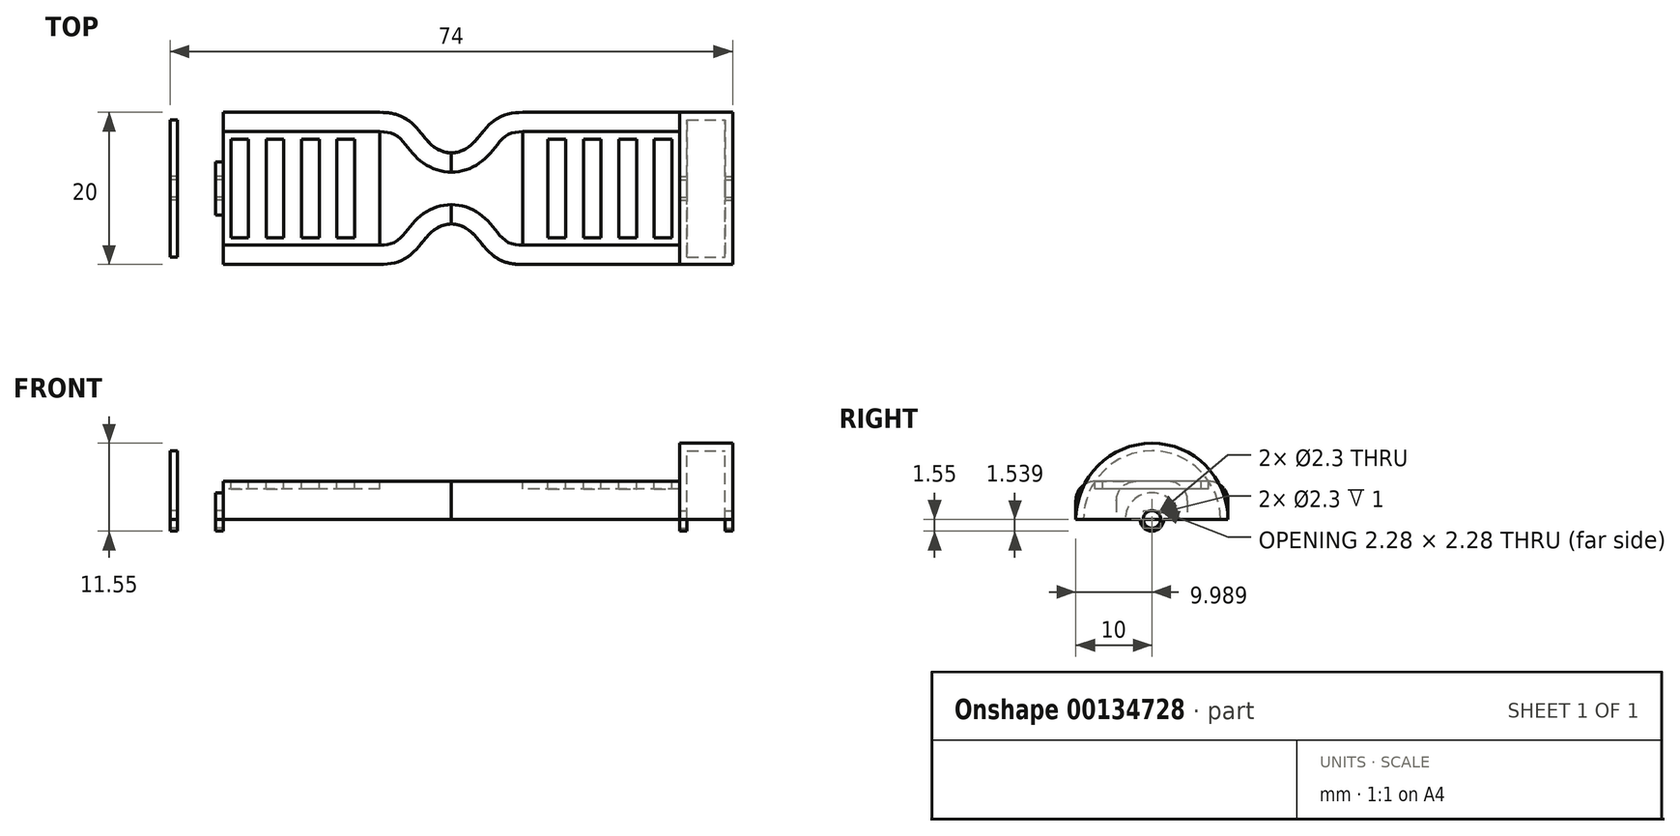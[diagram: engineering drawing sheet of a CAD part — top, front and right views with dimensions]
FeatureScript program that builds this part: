
annotation { "Feature Type Name" : "Feature", "Feature Type Description" : "" }
export const myFeature = defineFeature(function(context is Context, id is Id, definition is map)
    precondition{}
    {
        {
            var Q0;
            Q0=qCreatedBy(makeId("Top.planeOp"),FACE);
            var sketch = newSketch(context, id + "F0", { "sketchPlane" : qUnion([Q0])});
            skLineSegment(sketch, "E0.bottom", {"start": v(37, 10) * mm, "end": v(-37, 10) * mm});
            skLineSegment(sketch, "E0.top", {"start": v(37, -10) * mm, "end": v(-37, -10) * mm});
            skLineSegment(sketch, "E0.left", {"start": v(37, 10) * mm, "end": v(37, -10) * mm});
            skLineSegment(sketch, "E0.right", {"start": v(-37, 10) * mm, "end": v(-37, -10) * mm});
            skPoint(sketch, "E0.middle", {"position": v(0, 0) * mm});
            skLineSegment(sketch, "E1", {"start": v(30, 10) * mm, "end": v(30, -10) * mm});
            skLineSegment(sketch, "E2.MirrorCS", {"start": v(-30, 10) * mm, "end": v(-30, -10) * mm});
            skLineSegment(sketch, "E3", {"start": v(-9.38, 10) * mm, "end": v(-9.38, -10) * mm});
            skLineSegment(sketch, "E4.MirrorCS", {"start": v(9.38, 10) * mm, "end": v(9.38, -10) * mm});
            skFitSpline(sketch, "E5", {"points": [v(-9.38, 10) * mm, v(0, 4.67) * mm], "startDerivative": vector(17.64, 0) * mm, "endDerivative": vector(12.98, -0.7) * mm});
            skFitSpline(sketch, "E6.MirrorCS", {"points": [v(-9.38, -10) * mm, v(0, -4.67) * mm], "startDerivative": vector(17.64, 0) * mm, "endDerivative": vector(12.98, 0.7) * mm});
            skFitSpline(sketch, "E7.MirrorCS", {"points": [v(9.38, 10) * mm, v(0, 4.67) * mm], "startDerivative": vector(-17.64, 0) * mm, "endDerivative": vector(-12.98, -0.7) * mm});
            skFitSpline(sketch, "E8.MirrorCS", {"points": [v(9.38, -10) * mm, v(0, -4.67) * mm], "startDerivative": vector(-17.64, 0) * mm, "endDerivative": vector(-12.98, 0.7) * mm});
            skLineSegment(sketch, "E9", {"start": v(-37, 10) * mm, "end": v(-30, 10) * mm});
            skLineSegment(sketch, "E10", {"start": v(-30, -10) * mm, "end": v(-37, -10) * mm});
            skLineSegment(sketch, "E11.0", {"start": v(-31, -9) * mm, "end": v(-37, -9) * mm});
            skLineSegment(sketch, "E11.1", {"start": v(-31, 9) * mm, "end": v(-31, -9) * mm});
            skLineSegment(sketch, "E11.2", {"start": v(-37, 9) * mm, "end": v(-31, 9) * mm});
            skLineSegment(sketch, "E12", {"start": v(-36, 9) * mm, "end": v(-36, -9) * mm});
            skLineSegment(sketch, "E13.MirrorCS", {"start": v(36, 9) * mm, "end": v(36, -9) * mm});
            skLineSegment(sketch, "E14.MirrorCS", {"start": v(37, 9) * mm, "end": v(31, 9) * mm});
            skLineSegment(sketch, "E15.MirrorCS", {"start": v(31, 9) * mm, "end": v(31, -9) * mm});
            skLineSegment(sketch, "E16.MirrorCS", {"start": v(31, -9) * mm, "end": v(37, -9) * mm});
            skLineSegment(sketch, "E17", {"start": v(-37, 0) * mm, "end": v(37, 0) * mm});
            skLineSegment(sketch, "E18", {"start": v(-31, -3.5) * mm, "end": v(-16, -3.5) * mm});
            skLineSegment(sketch, "E19", {"start": v(-16, -3.5) * mm, "end": v(-16, 0) * mm});
            skLineSegment(sketch, "E20", {"start": v(-31, 0) * mm, "end": v(-31, -3.5) * mm});
            skLineSegment(sketch, "E21.MirrorCS", {"start": v(-31, 3.5) * mm, "end": v(-16, 3.5) * mm});
            skLineSegment(sketch, "E22.MirrorCS", {"start": v(-16, 3.5) * mm, "end": v(-16, 0) * mm});
            skLineSegment(sketch, "E23.MirrorCS", {"start": v(31, -3.5) * mm, "end": v(16, -3.5) * mm});
            skLineSegment(sketch, "E24.MirrorCS", {"start": v(16, -3.5) * mm, "end": v(16, 0) * mm});
            skLineSegment(sketch, "E25.MirrorCS", {"start": v(31, 3.5) * mm, "end": v(16, 3.5) * mm});
            skLineSegment(sketch, "E26.MirrorCS", {"start": v(16, 3.5) * mm, "end": v(16, 0) * mm});
            skLineSegment(sketch, "E27", {"start": v(-16, -3.5) * mm, "end": v(-12, -3.5) * mm});
            skLineSegment(sketch, "E28", {"start": v(-12, -3.5) * mm, "end": v(-12, 0) * mm});
            skLineSegment(sketch, "E29.MirrorCS", {"start": v(-12, 3.5) * mm, "end": v(-12, 0) * mm});
            skLineSegment(sketch, "E30.MirrorCS", {"start": v(-16, 3.5) * mm, "end": v(-12, 3.5) * mm});
            skLineSegment(sketch, "E31.MirrorCS", {"start": v(12, -3.5) * mm, "end": v(12, 0) * mm});
            skLineSegment(sketch, "E32.MirrorCS", {"start": v(16, -3.5) * mm, "end": v(12, -3.5) * mm});
            skLineSegment(sketch, "E33.MirrorCS", {"start": v(12, 3.5) * mm, "end": v(12, 0) * mm});
            skLineSegment(sketch, "E34.MirrorCS", {"start": v(16, 3.5) * mm, "end": v(12, 3.5) * mm});
            skLineSegment(sketch, "E35", {"start": v(-31, -2.3) * mm, "end": v(-16, -2.3) * mm});
            skLineSegment(sketch, "E36.MirrorCS", {"start": v(31, -2.3) * mm, "end": v(16, -2.3) * mm});
            skSolve(sketch);
        }
        {
            var Q0;
            {var subQ1=sQuery(id+"F0.wireOp",EDGE,"E6.MirrorCS");Q0=makeQuery(id+"F0.imprint","IMPRINT",FACE,{"disambiguationData":[TD([[makeQuery(id+"F0.imprint","IMPRINT",EDGE,{"derivedFrom":subQ1}),1.0]])]});}
            var Q1;
            {var subQ10=sQuery(id+"F0.wireOp",EDGE,"E27");Q1=makeQuery(id+"F0.imprint","IMPRINT",FACE,{"disambiguationData":[TD([[makeQuery(id+"F0.imprint","IMPRINT",EDGE,{"derivedFrom":subQ10}),-1.0]])]});}
            var Q2;
            {var subQ1=sQuery(id+"F0.wireOp",EDGE,"E5");Q2=makeQuery(id+"F0.imprint","IMPRINT",FACE,{"disambiguationData":[TD([[makeQuery(id+"F0.imprint","IMPRINT",EDGE,{"derivedFrom":subQ1}),-1.0]])]});}
            var Q3;
            {var subQ5=sQuery(id+"F0.wireOp",EDGE,"E31.MirrorCS");Q3=makeQuery(id+"F0.imprint","IMPRINT",FACE,{"disambiguationData":[TD([[makeQuery(id+"F0.imprint","IMPRINT",EDGE,{"derivedFrom":subQ5}),1.0]])]});}
            var Q4;
            {var subQ0=sQuery(id+"F0.wireOp",EDGE,"E29.MirrorCS");Q4=makeQuery(id+"F0.imprint","IMPRINT",FACE,{"disambiguationData":[TD([[makeQuery(id+"F0.imprint","IMPRINT",EDGE,{"derivedFrom":subQ0}),1.0]])]});}
            var Q5;
            {var subQ5=sQuery(id+"F0.wireOp",EDGE,"E33.MirrorCS");Q5=makeQuery(id+"F0.imprint","IMPRINT",FACE,{"disambiguationData":[TD([[makeQuery(id+"F0.imprint","IMPRINT",EDGE,{"derivedFrom":subQ5}),-1.0]])]});}
            var Q6;
            {var subQ5=sQuery(id+"F0.wireOp",EDGE,"E24.MirrorCS");Q6=makeQuery(id+"F0.imprint","IMPRINT",FACE,{"disambiguationData":[TD([[makeQuery(id+"F0.imprint","IMPRINT",EDGE,{"derivedFrom":subQ5}),-1.0]])]});}
            var Q7;
            {var subQ0=sQuery(id+"F0.wireOp",EDGE,"E24.MirrorCS");Q7=makeQuery(id+"F0.imprint","IMPRINT",FACE,{"disambiguationData":[TD([[makeQuery(id+"F0.imprint","IMPRINT",EDGE,{"derivedFrom":subQ0}),1.0]])]});}
            var Q8;
            {var subQ5=sQuery(id+"F0.wireOp",EDGE,"E26.MirrorCS");Q8=makeQuery(id+"F0.imprint","IMPRINT",FACE,{"disambiguationData":[TD([[makeQuery(id+"F0.imprint","IMPRINT",EDGE,{"derivedFrom":subQ5}),1.0]])]});}
            var Q9;
            {var subQ0=sQuery(id+"F0.wireOp",EDGE,"E26.MirrorCS");Q9=makeQuery(id+"F0.imprint","IMPRINT",FACE,{"disambiguationData":[TD([[makeQuery(id+"F0.imprint","IMPRINT",EDGE,{"derivedFrom":subQ0}),-1.0]])]});}
            var Q10;
            {var subQ5=sQuery(id+"F0.wireOp",EDGE,"E19");Q10=makeQuery(id+"F0.imprint","IMPRINT",FACE,{"disambiguationData":[TD([[makeQuery(id+"F0.imprint","IMPRINT",EDGE,{"derivedFrom":subQ5}),1.0]])]});}
            var Q11;
            {var subQ0=sQuery(id+"F0.wireOp",EDGE,"E19");Q11=makeQuery(id+"F0.imprint","IMPRINT",FACE,{"disambiguationData":[TD([[makeQuery(id+"F0.imprint","IMPRINT",EDGE,{"derivedFrom":subQ0}),-1.0]])]});}
            var Q12;
            {var subQ0=sQuery(id+"F0.wireOp",EDGE,"E22.MirrorCS");Q12=makeQuery(id+"F0.imprint","IMPRINT",FACE,{"disambiguationData":[TD([[makeQuery(id+"F0.imprint","IMPRINT",EDGE,{"derivedFrom":subQ0}),1.0]])]});}
            var Q13;
            {var subQ5=sQuery(id+"F0.wireOp",EDGE,"E22.MirrorCS");Q13=makeQuery(id+"F0.imprint","IMPRINT",FACE,{"disambiguationData":[TD([[makeQuery(id+"F0.imprint","IMPRINT",EDGE,{"derivedFrom":subQ5}),-1.0]])]});}
            extrude(context, id + "F1", {"entities" : qUnion([Q0, Q1, Q2, Q3, Q4, Q5, Q6, Q7, Q8, Q9, Q10, Q11, Q12, Q13]), "depth" : 5 * mm});
        }
        {
            var Q0;
            {var subQ0=sQuery(id+"F0.wireOp",EDGE,"E11.0");var subQ1=sQuery(id+"F0.wireOp",EDGE,"E0.right");var subQ2=makeQuery(id+"F0.imprint","INTERSECT",VERTEX,{"derivedFrom":[subQ1,subQ0]});Q0=makeQuery(id+"F0.imprint","IMPRINT",FACE,{"disambiguationData":[TD([[makeQuery(id+"F0.imprint","IMPRINT",EDGE,{"disambiguationData":[TD([[subQ2,1.0]])],"derivedFrom":subQ1}),1.0]])]});}
            var Q1;
            {var subQ0=sQuery(id+"F0.wireOp",EDGE,"E10");Q1=makeQuery(id+"F0.imprint","IMPRINT",FACE,{"disambiguationData":[TD([[makeQuery(id+"F0.imprint","IMPRINT",EDGE,{"derivedFrom":subQ0}),-1.0]])]});}
            var Q2;
            {var subQ0=sQuery(id+"F0.wireOp",EDGE,"E16.MirrorCS");var subQ1=sQuery(id+"F0.wireOp",EDGE,"E0.left");var subQ2=makeQuery(id+"F0.imprint","INTERSECT",VERTEX,{"derivedFrom":[subQ1,subQ0]});Q2=makeQuery(id+"F0.imprint","IMPRINT",FACE,{"disambiguationData":[TD([[makeQuery(id+"F0.imprint","IMPRINT",EDGE,{"disambiguationData":[TD([[subQ2,1.0]])],"derivedFrom":subQ1}),-1.0]])]});}
            var Q3;
            {var subQ6=sQuery(id+"F0.wireOp",EDGE,"E0.top");var subQ10=sQuery(id+"F0.wireOp",EDGE,"E0.left");var subQ11=makeQuery(id+"F0.imprint","INTERSECT",VERTEX,{"derivedFrom":[subQ6,subQ10]});Q3=makeQuery(id+"F0.imprint","IMPRINT",FACE,{"disambiguationData":[TD([[makeQuery(id+"F0.imprint","IMPRINT",EDGE,{"disambiguationData":[TD([[subQ11,-1.0]])],"derivedFrom":subQ6}),-1.0]])]});}
            var Q4;
            {var subQ0=sQuery(id+"F0.wireOp",EDGE,"E35");var subQ1=sQuery(id+"F0.wireOp",EDGE,"E2.MirrorCS");var subQ2=makeQuery(id+"F0.imprint","INTERSECT",VERTEX,{"derivedFrom":[subQ1,subQ0]});Q4=makeQuery(id+"F0.imprint","IMPRINT",FACE,{"disambiguationData":[TD([[makeQuery(id+"F0.imprint","IMPRINT",EDGE,{"disambiguationData":[TD([[subQ2,-1.0]])],"derivedFrom":subQ1}),-1.0]])]});}
            var Q5;
            {var subQ0=sQuery(id+"F0.wireOp",EDGE,"E17");var subQ1=sQuery(id+"F0.wireOp",EDGE,"E2.MirrorCS");var subQ2=makeQuery(id+"F0.imprint","INTERSECT",VERTEX,{"derivedFrom":[subQ1,subQ0]});Q5=makeQuery(id+"F0.imprint","IMPRINT",FACE,{"disambiguationData":[TD([[makeQuery(id+"F0.imprint","IMPRINT",EDGE,{"disambiguationData":[TD([[subQ2,-1.0]])],"derivedFrom":subQ1}),-1.0]])]});}
            var Q6;
            {var subQ0=sQuery(id+"F0.wireOp",EDGE,"E36.MirrorCS");var subQ1=sQuery(id+"F0.wireOp",EDGE,"E1");var subQ2=makeQuery(id+"F0.imprint","INTERSECT",VERTEX,{"derivedFrom":[subQ1,subQ0]});Q6=makeQuery(id+"F0.imprint","IMPRINT",FACE,{"disambiguationData":[TD([[makeQuery(id+"F0.imprint","IMPRINT",EDGE,{"disambiguationData":[TD([[subQ2,-1.0]])],"derivedFrom":subQ1}),1.0]])]});}
            var Q7;
            {var subQ0=sQuery(id+"F0.wireOp",EDGE,"E17");var subQ1=sQuery(id+"F0.wireOp",EDGE,"E1");var subQ2=makeQuery(id+"F0.imprint","INTERSECT",VERTEX,{"derivedFrom":[subQ1,subQ0]});Q7=makeQuery(id+"F0.imprint","IMPRINT",FACE,{"disambiguationData":[TD([[makeQuery(id+"F0.imprint","IMPRINT",EDGE,{"disambiguationData":[TD([[subQ2,-1.0]])],"derivedFrom":subQ1}),1.0]])]});}
            var Q8;
            Q8=sQuery(id+"F0.wireOp",EDGE,"E17");
            revolve(context, id + "F2", {"entities" : qUnion([Q0, Q1, Q2, Q3, Q4, Q5, Q6, Q7]), "axis" : qUnion([Q8]), "revolveType" : RevolveType.ONE_DIRECTION, "oppositeDirection" : true, "angle" : 180 * degree});
        }
        {
            var Q0;
            {var subQ0=sQuery(id+"F0.wireOp",EDGE,"E0.top");Q0=makeQuery(id+"F1.opExtrude","CAP_EDGE",EDGE,{"disambiguationData":[OSD([subQ0]),TDD([makeQuery(id+"F0.imprint","IMPRINT",EDGE,{"disambiguationData":[TD([[makeQuery(id+"F0.imprint","INTERSECT",VERTEX,{"derivedFrom":[subQ0,sQuery(id+"F0.wireOp",EDGE,"E2.MirrorCS"),sQuery(id+"F0.wireOp",EDGE,"E10")]}),1.0]])],"derivedFrom":subQ0})])],"isStart":false});}
            var Q1;
            Q1=makeQuery(id+"F1.opExtrude","CAP_EDGE",EDGE,{"disambiguationData":[OSD([sQuery(id+"F0.wireOp",EDGE,"E6.MirrorCS")])],"isStart":false});
            var Q2;
            Q2=makeQuery(id+"F1.opExtrude","CAP_EDGE",EDGE,{"disambiguationData":[OSD([sQuery(id+"F0.wireOp",EDGE,"E8.MirrorCS")])],"isStart":false});
            var Q3;
            {var subQ0=sQuery(id+"F0.wireOp",EDGE,"E0.bottom");Q3=makeQuery(id+"F1.opExtrude","CAP_EDGE",EDGE,{"disambiguationData":[OSD([subQ0]),TDD([makeQuery(id+"F0.imprint","IMPRINT",EDGE,{"disambiguationData":[TD([[makeQuery(id+"F0.imprint","INTERSECT",VERTEX,{"derivedFrom":[subQ0,sQuery(id+"F0.wireOp",EDGE,"E1")]}),-1.0]])],"derivedFrom":subQ0})])],"isStart":false});}
            var Q4;
            Q4=makeQuery(id+"F1.opExtrude","CAP_EDGE",EDGE,{"disambiguationData":[OSD([sQuery(id+"F0.wireOp",EDGE,"E7.MirrorCS")])],"isStart":false});
            var Q5;
            Q5=makeQuery(id+"F1.opExtrude","CAP_EDGE",EDGE,{"disambiguationData":[OSD([sQuery(id+"F0.wireOp",EDGE,"E5")])],"isStart":false});
            var Q6;
            {var subQ0=sQuery(id+"F0.wireOp",EDGE,"E0.bottom");Q6=makeQuery(id+"F1.opExtrude","CAP_EDGE",EDGE,{"disambiguationData":[OSD([subQ0]),TDD([makeQuery(id+"F0.imprint","IMPRINT",EDGE,{"disambiguationData":[TD([[makeQuery(id+"F0.imprint","INTERSECT",VERTEX,{"derivedFrom":[subQ0,sQuery(id+"F0.wireOp",EDGE,"E2.MirrorCS"),sQuery(id+"F0.wireOp",EDGE,"E9")]}),1.0]])],"derivedFrom":subQ0})])],"isStart":false});}
            var Q7;
            {var subQ0=sQuery(id+"F0.wireOp",EDGE,"E0.top");Q7=makeQuery(id+"F1.opExtrude","CAP_EDGE",EDGE,{"disambiguationData":[OSD([subQ0]),TDD([makeQuery(id+"F0.imprint","IMPRINT",EDGE,{"disambiguationData":[TD([[makeQuery(id+"F0.imprint","INTERSECT",VERTEX,{"derivedFrom":[subQ0,sQuery(id+"F0.wireOp",EDGE,"E1")]}),-1.0]])],"derivedFrom":subQ0})])],"isStart":false});}
            fillet(context, id + "F3", {"entities" : qUnion([Q0, Q1, Q2, Q3, Q4, Q5, Q6, Q7]), "radius" : 2.54 * mm, "tangentPropagation" : true, "allowEdgeOverflow" : false});
        }
        {
            var Q0;
            Q0=makeQuery(id+"F1.opExtrude","CAP_FACE",FACE,{"disambiguationData":[OSD([sQuery(id+"F0.wireOp",EDGE,"E0.bottom"),sQuery(id+"F0.wireOp",EDGE,"E0.top"),sQuery(id+"F0.wireOp",EDGE,"E1"),sQuery(id+"F0.wireOp",EDGE,"E2.MirrorCS"),sQuery(id+"F0.wireOp",EDGE,"E5"),sQuery(id+"F0.wireOp",EDGE,"E6.MirrorCS"),sQuery(id+"F0.wireOp",EDGE,"E7.MirrorCS"),sQuery(id+"F0.wireOp",EDGE,"E8.MirrorCS")])],"isStart":false});
            var sketch = newSketch(context, id + "F4", { "sketchPlane" : qUnion([Q0])});
            skLineSegment(sketch, "E37.bottom", {"start": v(9.38, 7.46) * mm, "end": v(30, 7.46) * mm});
            skLineSegment(sketch, "E37.top", {"start": v(9.38, -7.46) * mm, "end": v(30, -7.46) * mm});
            skLineSegment(sketch, "E37.left", {"start": v(9.38, 7.46) * mm, "end": v(9.38, -7.46) * mm});
            skLineSegment(sketch, "E37.right", {"start": v(30, 7.46) * mm, "end": v(30, -7.46) * mm});
            skLineSegment(sketch, "E38.0", {"start": v(10.38, 6.46) * mm, "end": v(10.38, -6.46) * mm});
            skLineSegment(sketch, "E38.1", {"start": v(10.38, 6.46) * mm, "end": v(29, 6.46) * mm});
            skLineSegment(sketch, "E38.2", {"start": v(29, 6.46) * mm, "end": v(29, -6.46) * mm});
            skLineSegment(sketch, "E38.3", {"start": v(10.38, -6.46) * mm, "end": v(29, -6.46) * mm});
            skLineSegment(sketch, "E39", {"start": v(10.38, 0) * mm, "end": v(29, 0) * mm});
            skLineSegment(sketch, "E40", {"start": v(19.7, 6.46) * mm, "end": v(19.7, -6.46) * mm});
            skLineSegment(sketch, "E41", {"start": v(19.7, 6.46) * mm, "end": v(29, 6.46) * mm});
            skLineSegment(sketch, "E42", {"start": v(29, -6.46) * mm, "end": v(19.7, -6.46) * mm});
            skLineSegment(sketch, "E43", {"start": v(10.38, -6.46) * mm, "end": v(19.7, -6.46) * mm});
            skLineSegment(sketch, "E44", {"start": v(19.7, 6.46) * mm, "end": v(10.38, 6.46) * mm});
            skLineSegment(sketch, "E45", {"start": v(24.35, 6.46) * mm, "end": v(24.35, -6.46) * mm});
            skLineSegment(sketch, "E46", {"start": v(15.04, -6.46) * mm, "end": v(15.04, 6.46) * mm});
            skLineSegment(sketch, "E47", {"start": v(10.38, 6.46) * mm, "end": v(15.04, 6.46) * mm});
            skLineSegment(sketch, "E48", {"start": v(15.04, 6.46) * mm, "end": v(19.7, 6.46) * mm});
            skLineSegment(sketch, "E49", {"start": v(19.7, 6.46) * mm, "end": v(24.35, 6.46) * mm});
            skLineSegment(sketch, "E50", {"start": v(24.35, 6.46) * mm, "end": v(29, 6.46) * mm});
            skLineSegment(sketch, "E51", {"start": v(29, -6.46) * mm, "end": v(24.35, -6.46) * mm});
            skLineSegment(sketch, "E52", {"start": v(24.35, -6.46) * mm, "end": v(19.7, -6.46) * mm});
            skLineSegment(sketch, "E53", {"start": v(19.7, -6.46) * mm, "end": v(15.04, -6.46) * mm});
            skLineSegment(sketch, "E54", {"start": v(15.04, -6.46) * mm, "end": v(10.38, -6.46) * mm});
            skLineSegment(sketch, "E55", {"start": v(12.71, 6.46) * mm, "end": v(12.71, -6.46) * mm});
            skLineSegment(sketch, "E56", {"start": v(17.37, 6.46) * mm, "end": v(17.37, -6.46) * mm});
            skLineSegment(sketch, "E57", {"start": v(22.02, -6.46) * mm, "end": v(22.02, 6.46) * mm});
            skLineSegment(sketch, "E58", {"start": v(26.67, 6.46) * mm, "end": v(26.67, -6.46) * mm});
            skLineSegment(sketch, "E59.MirrorCS", {"start": v(-9.38, 7.46) * mm, "end": v(-9.38, -7.46) * mm});
            skLineSegment(sketch, "E60.MirrorCS", {"start": v(-29, 6.46) * mm, "end": v(-29, -6.46) * mm});
            skLineSegment(sketch, "E61.MirrorCS", {"start": v(-10.38, 0) * mm, "end": v(-29, 0) * mm});
            skLineSegment(sketch, "E62.MirrorCS", {"start": v(-19.7, 6.46) * mm, "end": v(-19.7, -6.46) * mm});
            skLineSegment(sketch, "E63.MirrorCS", {"start": v(-10.38, 6.46) * mm, "end": v(-10.38, -6.46) * mm});
            skLineSegment(sketch, "E64.MirrorCS", {"start": v(-22.02, -6.46) * mm, "end": v(-22.02, 6.46) * mm});
            skLineSegment(sketch, "E65.MirrorCS", {"start": v(-12.71, 6.46) * mm, "end": v(-12.71, -6.46) * mm});
            skLineSegment(sketch, "E66.MirrorCS", {"start": v(-15.04, -6.46) * mm, "end": v(-15.04, 6.46) * mm});
            skLineSegment(sketch, "E67.MirrorCS", {"start": v(-26.67, 6.46) * mm, "end": v(-26.67, -6.46) * mm});
            skLineSegment(sketch, "E68.MirrorCS", {"start": v(-17.37, 6.46) * mm, "end": v(-17.37, -6.46) * mm});
            skLineSegment(sketch, "E69.MirrorCS", {"start": v(-24.35, 6.46) * mm, "end": v(-24.35, -6.46) * mm});
            skLineSegment(sketch, "E70.MirrorCS", {"start": v(-10.38, 6.46) * mm, "end": v(-15.04, 6.46) * mm});
            skLineSegment(sketch, "E71.MirrorCS", {"start": v(-19.7, 6.46) * mm, "end": v(-29, 6.46) * mm});
            skLineSegment(sketch, "E72.MirrorCS", {"start": v(-15.04, 6.46) * mm, "end": v(-19.7, 6.46) * mm});
            skLineSegment(sketch, "E73.MirrorCS", {"start": v(-19.7, 6.46) * mm, "end": v(-10.38, 6.46) * mm});
            skLineSegment(sketch, "E74.MirrorCS", {"start": v(-24.35, 6.46) * mm, "end": v(-29, 6.46) * mm});
            skLineSegment(sketch, "E75.MirrorCS", {"start": v(-19.7, 6.46) * mm, "end": v(-24.35, 6.46) * mm});
            skLineSegment(sketch, "E76.MirrorCS", {"start": v(-10.38, 6.46) * mm, "end": v(-29, 6.46) * mm});
            skLineSegment(sketch, "E77.MirrorCS", {"start": v(-29, -6.46) * mm, "end": v(-19.7, -6.46) * mm});
            skLineSegment(sketch, "E78.MirrorCS", {"start": v(-10.38, -6.46) * mm, "end": v(-19.7, -6.46) * mm});
            skLineSegment(sketch, "E79.MirrorCS", {"start": v(-19.7, -6.46) * mm, "end": v(-15.04, -6.46) * mm});
            skLineSegment(sketch, "E80.MirrorCS", {"start": v(-24.35, -6.46) * mm, "end": v(-19.7, -6.46) * mm});
            skLineSegment(sketch, "E81.MirrorCS", {"start": v(-29, -6.46) * mm, "end": v(-24.35, -6.46) * mm});
            skLineSegment(sketch, "E82.MirrorCS", {"start": v(-15.04, -6.46) * mm, "end": v(-10.38, -6.46) * mm});
            skLineSegment(sketch, "E83.MirrorCS", {"start": v(-10.38, -6.46) * mm, "end": v(-29, -6.46) * mm});
            skSolve(sketch);
        }
        {
            var Q0;
            Q0=makeQuery(id+"F4.imprint","IMPRINT",FACE,{"disambiguationData":[TD([[makeQuery(id+"F4.imprint","IMPRINT",EDGE,{"derivedFrom":sQuery(id+"F4.wireOp",EDGE,"E37.bottom")}),1.0]])]});
            var Q1;
            {var subQ0=sQuery(id+"F4.wireOp",EDGE,"E54");var subQ1=sQuery(id+"F4.wireOp",EDGE,"E38.0");var subQ2=makeQuery(id+"F4.imprint","INTERSECT",VERTEX,{"derivedFrom":[subQ1,subQ0]});Q1=makeQuery(id+"F4.imprint","IMPRINT",FACE,{"disambiguationData":[TD([[makeQuery(id+"F4.imprint","IMPRINT",EDGE,{"disambiguationData":[TD([[subQ2,1.0]])],"derivedFrom":subQ1}),1.0]])]});}
            var Q2;
            {var subQ0=sQuery(id+"F4.wireOp",EDGE,"E47");var subQ1=sQuery(id+"F4.wireOp",EDGE,"E38.0");var subQ2=makeQuery(id+"F4.imprint","INTERSECT",VERTEX,{"derivedFrom":[subQ1,subQ0]});Q2=makeQuery(id+"F4.imprint","IMPRINT",FACE,{"disambiguationData":[TD([[makeQuery(id+"F4.imprint","IMPRINT",EDGE,{"disambiguationData":[TD([[subQ2,-1.0]])],"derivedFrom":subQ1}),1.0]])]});}
            var Q3;
            {var subQ0=sQuery(id+"F4.wireOp",EDGE,"E46");var subQ1=sQuery(id+"F4.wireOp",EDGE,"E39");var subQ2=makeQuery(id+"F4.imprint","INTERSECT",VERTEX,{"derivedFrom":[subQ1,subQ0]});Q3=makeQuery(id+"F4.imprint","IMPRINT",FACE,{"disambiguationData":[TD([[makeQuery(id+"F4.imprint","IMPRINT",EDGE,{"disambiguationData":[TD([[subQ2,-1.0]])],"derivedFrom":subQ1}),1.0]])]});}
            var Q4;
            {var subQ0=sQuery(id+"F4.wireOp",EDGE,"E46");var subQ1=sQuery(id+"F4.wireOp",EDGE,"E39");var subQ2=makeQuery(id+"F4.imprint","INTERSECT",VERTEX,{"derivedFrom":[subQ1,subQ0]});Q4=makeQuery(id+"F4.imprint","IMPRINT",FACE,{"disambiguationData":[TD([[makeQuery(id+"F4.imprint","IMPRINT",EDGE,{"disambiguationData":[TD([[subQ2,-1.0]])],"derivedFrom":subQ1}),-1.0]])]});}
            var Q5;
            {var subQ0=sQuery(id+"F4.wireOp",EDGE,"E40");var subQ1=sQuery(id+"F4.wireOp",EDGE,"E39");var subQ2=makeQuery(id+"F4.imprint","INTERSECT",VERTEX,{"derivedFrom":[subQ1,subQ0]});Q5=makeQuery(id+"F4.imprint","IMPRINT",FACE,{"disambiguationData":[TD([[makeQuery(id+"F4.imprint","IMPRINT",EDGE,{"disambiguationData":[TD([[subQ2,-1.0]])],"derivedFrom":subQ1}),-1.0]])]});}
            var Q6;
            {var subQ0=sQuery(id+"F4.wireOp",EDGE,"E40");var subQ1=sQuery(id+"F4.wireOp",EDGE,"E39");var subQ2=makeQuery(id+"F4.imprint","INTERSECT",VERTEX,{"derivedFrom":[subQ1,subQ0]});Q6=makeQuery(id+"F4.imprint","IMPRINT",FACE,{"disambiguationData":[TD([[makeQuery(id+"F4.imprint","IMPRINT",EDGE,{"disambiguationData":[TD([[subQ2,-1.0]])],"derivedFrom":subQ1}),1.0]])]});}
            var Q7;
            {var subQ0=sQuery(id+"F4.wireOp",EDGE,"E45");var subQ1=sQuery(id+"F4.wireOp",EDGE,"E39");var subQ2=makeQuery(id+"F4.imprint","INTERSECT",VERTEX,{"derivedFrom":[subQ1,subQ0]});Q7=makeQuery(id+"F4.imprint","IMPRINT",FACE,{"disambiguationData":[TD([[makeQuery(id+"F4.imprint","IMPRINT",EDGE,{"disambiguationData":[TD([[subQ2,-1.0]])],"derivedFrom":subQ1}),1.0]])]});}
            var Q8;
            {var subQ0=sQuery(id+"F4.wireOp",EDGE,"E45");var subQ1=sQuery(id+"F4.wireOp",EDGE,"E39");var subQ2=makeQuery(id+"F4.imprint","INTERSECT",VERTEX,{"derivedFrom":[subQ1,subQ0]});Q8=makeQuery(id+"F4.imprint","IMPRINT",FACE,{"disambiguationData":[TD([[makeQuery(id+"F4.imprint","IMPRINT",EDGE,{"disambiguationData":[TD([[subQ2,-1.0]])],"derivedFrom":subQ1}),-1.0]])]});}
            var Q9;
            Q9=makeQuery(id+"F4.imprint","IMPRINT",FACE,{"disambiguationData":[TD([[makeQuery(id+"F4.imprint","IMPRINT",EDGE,{"derivedFrom":sQuery(id+"F4.wireOp",EDGE,"E59.MirrorCS")}),-1.0]])]});
            var Q10;
            {var subQ0=sQuery(id+"F4.wireOp",EDGE,"E63.MirrorCS");var subQ1=sQuery(id+"F4.wireOp",EDGE,"E61.MirrorCS");var subQ2=makeQuery(id+"F4.imprint","INTERSECT",VERTEX,{"derivedFrom":[subQ1,subQ0]});Q10=makeQuery(id+"F4.imprint","IMPRINT",FACE,{"disambiguationData":[TD([[makeQuery(id+"F4.imprint","IMPRINT",EDGE,{"disambiguationData":[TD([[subQ2,-1.0]])],"derivedFrom":subQ1}),-1.0]])]});}
            var Q11;
            {var subQ0=sQuery(id+"F4.wireOp",EDGE,"E63.MirrorCS");var subQ1=sQuery(id+"F4.wireOp",EDGE,"E61.MirrorCS");var subQ2=makeQuery(id+"F4.imprint","INTERSECT",VERTEX,{"derivedFrom":[subQ1,subQ0]});Q11=makeQuery(id+"F4.imprint","IMPRINT",FACE,{"disambiguationData":[TD([[makeQuery(id+"F4.imprint","IMPRINT",EDGE,{"disambiguationData":[TD([[subQ2,-1.0]])],"derivedFrom":subQ1}),1.0]])]});}
            var Q12;
            {var subQ0=sQuery(id+"F4.wireOp",EDGE,"E66.MirrorCS");var subQ1=sQuery(id+"F4.wireOp",EDGE,"E61.MirrorCS");var subQ2=makeQuery(id+"F4.imprint","INTERSECT",VERTEX,{"derivedFrom":[subQ1,subQ0]});Q12=makeQuery(id+"F4.imprint","IMPRINT",FACE,{"disambiguationData":[TD([[makeQuery(id+"F4.imprint","IMPRINT",EDGE,{"disambiguationData":[TD([[subQ2,-1.0]])],"derivedFrom":subQ1}),1.0]])]});}
            var Q13;
            {var subQ0=sQuery(id+"F4.wireOp",EDGE,"E66.MirrorCS");var subQ1=sQuery(id+"F4.wireOp",EDGE,"E61.MirrorCS");var subQ2=makeQuery(id+"F4.imprint","INTERSECT",VERTEX,{"derivedFrom":[subQ1,subQ0]});Q13=makeQuery(id+"F4.imprint","IMPRINT",FACE,{"disambiguationData":[TD([[makeQuery(id+"F4.imprint","IMPRINT",EDGE,{"disambiguationData":[TD([[subQ2,-1.0]])],"derivedFrom":subQ1}),-1.0]])]});}
            var Q14;
            {var subQ0=sQuery(id+"F4.wireOp",EDGE,"E62.MirrorCS");var subQ1=sQuery(id+"F4.wireOp",EDGE,"E61.MirrorCS");var subQ2=makeQuery(id+"F4.imprint","INTERSECT",VERTEX,{"derivedFrom":[subQ1,subQ0]});Q14=makeQuery(id+"F4.imprint","IMPRINT",FACE,{"disambiguationData":[TD([[makeQuery(id+"F4.imprint","IMPRINT",EDGE,{"disambiguationData":[TD([[subQ2,-1.0]])],"derivedFrom":subQ1}),1.0]])]});}
            var Q15;
            {var subQ0=sQuery(id+"F4.wireOp",EDGE,"E62.MirrorCS");var subQ1=sQuery(id+"F4.wireOp",EDGE,"E61.MirrorCS");var subQ2=makeQuery(id+"F4.imprint","INTERSECT",VERTEX,{"derivedFrom":[subQ1,subQ0]});Q15=makeQuery(id+"F4.imprint","IMPRINT",FACE,{"disambiguationData":[TD([[makeQuery(id+"F4.imprint","IMPRINT",EDGE,{"disambiguationData":[TD([[subQ2,-1.0]])],"derivedFrom":subQ1}),-1.0]])]});}
            var Q16;
            {var subQ0=sQuery(id+"F4.wireOp",EDGE,"E69.MirrorCS");var subQ1=sQuery(id+"F4.wireOp",EDGE,"E61.MirrorCS");var subQ2=makeQuery(id+"F4.imprint","INTERSECT",VERTEX,{"derivedFrom":[subQ1,subQ0]});Q16=makeQuery(id+"F4.imprint","IMPRINT",FACE,{"disambiguationData":[TD([[makeQuery(id+"F4.imprint","IMPRINT",EDGE,{"disambiguationData":[TD([[subQ2,-1.0]])],"derivedFrom":subQ1}),1.0]])]});}
            var Q17;
            {var subQ0=sQuery(id+"F4.wireOp",EDGE,"E69.MirrorCS");var subQ1=sQuery(id+"F4.wireOp",EDGE,"E61.MirrorCS");var subQ2=makeQuery(id+"F4.imprint","INTERSECT",VERTEX,{"derivedFrom":[subQ1,subQ0]});Q17=makeQuery(id+"F4.imprint","IMPRINT",FACE,{"disambiguationData":[TD([[makeQuery(id+"F4.imprint","IMPRINT",EDGE,{"disambiguationData":[TD([[subQ2,-1.0]])],"derivedFrom":subQ1}),-1.0]])]});}
            extrude(context, id + "F5", {"entities" : qUnion([Q0, Q1, Q2, Q3, Q4, Q5, Q6, Q7, Q8, Q9, Q10, Q11, Q12, Q13, Q14, Q15, Q16, Q17]), "operationType" : NewBodyOperationType.REMOVE, "oppositeDirection" : true, "depth" : 1 * mm});
        }
        {
            var Q0;
            Q0=makeQuery(id+"F2.opRevolve","SWEPT_FACE",FACE,{"disambiguationData":[OSD([sQuery(id+"F0.wireOp",EDGE,"E0.right")])]});
            var sketch = newSketch(context, id + "F6", { "sketchPlane" : qUnion([Q0])});
            skCircle(sketch, "E84", {"center": v(0, 0) * mm, "radius": 1.15 * mm});
            skCircle(sketch, "E85", {"center": v(0, 0) * mm, "radius": 1.55 * mm});
            skSolve(sketch);
        }
        {
            var Q0;
            {var subQ0=sQuery(id+"F6.wireOp",EDGE,"E84");var subQ1=makeQuery(id+"F2.opRevolve","CAP_EDGE",EDGE,{"disambiguationData":[OSD([sQuery(id+"F0.wireOp",EDGE,"E0.right")])],"isStart":false});var subQ2=makeQuery(id+"F6.imprint","INTERSECT",VERTEX,{"disambiguationData":[OD(0.0)],"derivedFrom":[subQ1,subQ0]});Q0=makeQuery(id+"F6.imprint","IMPRINT",FACE,{"disambiguationData":[TD([[makeQuery(id+"F6.imprint","IMPRINT",EDGE,{"disambiguationData":[TD([[subQ2,1.0]])],"derivedFrom":subQ0}),-1.0]])]});}
            extrude(context, id + "F7", {"entities" : qUnion([Q0]), "operationType" : NewBodyOperationType.ADD, "oppositeDirection" : true, "depth" : 7 * mm});
        }
        {
            var Q0;
            {var subQ0=sQuery(id+"F6.wireOp",EDGE,"E84");var subQ1=makeQuery(id+"F2.opRevolve","CAP_EDGE",EDGE,{"disambiguationData":[OSD([sQuery(id+"F0.wireOp",EDGE,"E0.right")])],"isStart":false});var subQ2=makeQuery(id+"F6.imprint","INTERSECT",VERTEX,{"disambiguationData":[OD(0.0)],"derivedFrom":[subQ1,subQ0]});Q0=makeQuery(id+"F6.imprint","IMPRINT",FACE,{"disambiguationData":[TD([[makeQuery(id+"F6.imprint","IMPRINT",EDGE,{"disambiguationData":[TD([[subQ2,-1.0]])],"derivedFrom":subQ0}),1.0]])]});}
            extrude(context, id + "F8", {"entities" : qUnion([Q0]), "operationType" : NewBodyOperationType.REMOVE, "oppositeDirection" : true, "depth" : 7 * mm});
        }
        {
            var Q0;
            {var subQ2=sQuery(id+"F0.wireOp",EDGE,"E11.1");var subQ6=sQuery(id+"F0.wireOp",EDGE,"E11.0");var subQ8=makeQuery(id+"F0.imprint","INTERSECT",VERTEX,{"derivedFrom":[subQ6,subQ2]});Q0=makeQuery(id+"F0.imprint","IMPRINT",FACE,{"disambiguationData":[TD([[makeQuery(id+"F0.imprint","IMPRINT",EDGE,{"disambiguationData":[TD([[subQ8,-1.0]])],"derivedFrom":subQ6}),-1.0]])]});}
            var Q1;
            Q1=sQuery(id+"F0.wireOp",EDGE,"E17");
            revolve(context, id + "F9", {"operationType" : NewBodyOperationType.REMOVE, "entities" : qUnion([Q0]), "axis" : qUnion([Q1]), "revolveType" : RevolveType.FULL, "oppositeDirection" : true});
        }
        {
            var Q0;
            Q0=makeQuery(id+"F2.opRevolve","SWEPT_FACE",FACE,{"disambiguationData":[OSD([sQuery(id+"F0.wireOp",EDGE,"E0.left")])]});
            var sketch = newSketch(context, id + "F10", { "sketchPlane" : qUnion([Q0])});
            skCircle(sketch, "E86", {"center": v(0, 0) * mm, "radius": 1.55 * mm});
            skCircle(sketch, "E87", {"center": v(0, 0) * mm, "radius": 1.15 * mm});
            skSolve(sketch);
        }
        {
            var Q0;
            {var subQ0=sQuery(id+"F10.wireOp",EDGE,"E86");var subQ1=makeQuery(id+"F2.opRevolve","CAP_EDGE",EDGE,{"disambiguationData":[OSD([sQuery(id+"F0.wireOp",EDGE,"E0.left")])],"isStart":false});var subQ2=makeQuery(id+"F10.imprint","INTERSECT",VERTEX,{"disambiguationData":[OD(0.0)],"derivedFrom":[subQ1,subQ0]});Q0=makeQuery(id+"F10.imprint","IMPRINT",FACE,{"disambiguationData":[TD([[makeQuery(id+"F10.imprint","IMPRINT",EDGE,{"disambiguationData":[TD([[subQ2,-1.0]])],"derivedFrom":subQ0}),1.0]])]});}
            extrude(context, id + "F11", {"entities" : qUnion([Q0]), "operationType" : NewBodyOperationType.ADD, "oppositeDirection" : true, "depth" : 7 * mm});
        }
        {
            var Q0;
            {var subQ0=sQuery(id+"F10.wireOp",EDGE,"E87");var subQ1=makeQuery(id+"F2.opRevolve","CAP_EDGE",EDGE,{"disambiguationData":[OSD([sQuery(id+"F0.wireOp",EDGE,"E0.left")])],"isStart":false});var subQ2=makeQuery(id+"F10.imprint","INTERSECT",VERTEX,{"disambiguationData":[OD(0.0)],"derivedFrom":[subQ1,subQ0]});Q0=makeQuery(id+"F10.imprint","IMPRINT",FACE,{"disambiguationData":[TD([[makeQuery(id+"F10.imprint","IMPRINT",EDGE,{"disambiguationData":[TD([[subQ2,1.0]])],"derivedFrom":subQ0}),1.0]])]});}
            extrude(context, id + "F12", {"entities" : qUnion([Q0]), "operationType" : NewBodyOperationType.REMOVE, "oppositeDirection" : true, "depth" : 7 * mm});
        }
        {
            var Q0;
            {var subQ4=sQuery(id+"F0.wireOp",EDGE,"E14.MirrorCS");var subQ6=sQuery(id+"F0.wireOp",EDGE,"E13.MirrorCS");var subQ7=makeQuery(id+"F0.imprint","INTERSECT",VERTEX,{"derivedFrom":[subQ6,subQ4]});Q0=makeQuery(id+"F0.imprint","IMPRINT",FACE,{"disambiguationData":[TD([[makeQuery(id+"F0.imprint","IMPRINT",EDGE,{"disambiguationData":[TD([[subQ7,-1.0]])],"derivedFrom":subQ6}),-1.0]])]});}
            var Q1;
            Q1=sQuery(id+"F0.wireOp",EDGE,"E17");
            revolve(context, id + "F13", {"operationType" : NewBodyOperationType.REMOVE, "entities" : qUnion([Q0]), "axis" : qUnion([Q1]), "revolveType" : RevolveType.FULL, "oppositeDirection" : true});
        }
    });
